# Revit family: IS_Gusto_BD420_BIM_NL
name_source: partatom
category: Plumbing Fixtures
units: mm (PartAtom-declared; Revit-internal decimal feet)

## family parameters
Always vertical = No
Cut with Voids When Loaded = No
OmniClass Number = 23.45.55.17
OmniClass Title = Mixing Faucets
Part Type = Normal
Room Calculation Point = No
Round Connector Dimension = Use Diameter
Shared = No
Work Plane-Based = No

## types (5) — shared parameters
Accessories = https://www.idealstandard.nl
Afmetingen = 115 x 275 x 333 mm
AfstandsEenheid = Millimeter
AreaUnits = millimetres
AssetType = Fixed
Auteur = Ideal Standard
BIMObjectName = IS_IdealStandard_Sinktaps_Gusto_BD420
BIMobject category = Taps & Mixers
BIMobject category code = sanitary-taps-mixers
BIMobject main category = Sanitary
BIMobject main category code = sanitary
Bedieningkraan = Einhebel
Bedieningkraanwerk = Einhebel
BeschrijvingBovenkantKraan = 2 Funktionen
Beschrijvinggarantie = Herstellergarantie
Bestanddelen = https://www.idealstandard.nl
BimObjectNaam = IS_IdealStandard_Sinktaps_Gusto_BD420
Brand = Ideal Standard
Brand url = http://www.idealstandard.nl
Breedte = 114.50873
Category = Taps & Mixers
ConnectionType = Plumbing
CurrencyUnit = €
CurrentRevision = 1
Date of publishing = 19/08/2022
Diepte = 275 mm
DurationUnit = Years
DuurEenheid = Jahre
Edition number = 1
ExpectedLife = 5
FaucetFunction = Sink Mixer
FaucetOperation = Single Lever Sink Mixer
FaucetTopDescription = Single lever
FaucetType = Sink Mixer
Functiekraanwerk = Küchenmischer
GTIN code = https://3800861108900
Garantieunits = Jahre
Help = https://www.idealstandard.nl
Hoogte = 333.311406525318
Hulp = https://www.idealstandard.nl
IFC Classification = Sanitary Terminal
Installatieinstructies = https://www.idealstandard.nl
Installation instructions = https://www.idealstandard.nl
InstallationInstructions = https://www.idealstandard.nl
Lengte = 275 mm
LinearUnits = millimetres
MaintenanceInformation = https://www.idealstandard.nl
Manufacturer = Ideal Standard
Manufacturer name = Ideal Standard
ManufacturerURL = http://www.idealstandard.nl
Masterformat 2014 Code = 22 41 16.16
Masterformat 2014 Description = Residential Sink
Materiaal = Messing
Material = Brass
Material main = Brass
Merk = Ideal Standard
NBS Reference Code = 45-35-70/345
NBS Reference Description = Water supply fittings for sinks
Name = Sinktaps_Gusto_BD420_IdealStandard
NettWeight = 3.04 Kg
Nettogewicht = 3.04
NominalDepth = 275 mm
NominalHeight = 333 mm
NominalLength = 275 mm
NominalWidth = 115 mm
Normen = Sinktaps_Gusto_BD420_IdealStandard
OmniClass Code = 23-31 11 00
OmniClass Description = Faucets
OppervlakteEenheid = Millimeter
PredefinedType = Taps & Mixers
Product Guid = 19f92fd7-092d-42a8-8991-9b57957d70f6
Product SKU = BD420
Product certification = https://www.idealstandard.nl
Product data url = https://bimobject.com
Product family = Gusto
Product group = Taps & Mixers
Product name = GUSTO SLIM SINK MIXER P/O 2 FUNTIONS BLUE START
Product url = https://www.idealstandard.nl
ProductInformation = https://www.idealstandard.nl
Productinformatie = https://www.idealstandard.nl
QR code = http://bimobject.com
Revisie = 1
Shape = Cylindrical
Size = 115 x 275 x 333 mm
Space = Internal
SpareParts = https://www.idealstandard.nl
Technical description = https://www.idealstandard.nl
Telefoonnummer = (0228) 521-580
Toepassing = Küchenmischer
Type Comments = Plumbing
Typeconnectie = Installation
Typekraanwerk = Einhebelmischer
UNSPSC Code = 301815
URL = https://www.idealstandard.nl
Uniclass 2015 Code = Pr_40_20_87_82
Uniclass 2015 Name = Sink manual water supply sets
Uniclass2015Beschrijving = Sink manual water supply sets
Uniclass2015Code = Pr_40_20_87_84
Uniclass2015Referentie = Pr_40_20_87_82
Uniclass2015Title = Sink taps
Uniclass2015Version = v1.26
Urlproducent = https://www.idealstandard.nl
ValutaEenheid = Euro
Versie = 1
Version = 1
VolumeUnits = Liters
Volumeunits = Liter
Vorm = Zylinder
WRASURL = https://www.wrasapprovals.co.uk
WarrantyDescription = manufacturer warranty
WarrantyDurationParts = 5
WarrantyDurationUnit = Years
WarrantyStartDate = 19/08/2022
Weight Net (Kg) = 3.04
Wisselstukken = https://www.idealstandard.nl
Youtube clip = https://www.youtube.com
zero-valued in all types: BrutoGewicht, Cost, Vervangingskosten

## per-type parameters (varying)
| type | Afwerking | Artikelnummer | Artikelomschrijving | Artikelreferentie | BarCode | Barcode | Color | Description | Eigenschappen | Features | Finish | Kleur | MainColor | Model | ModelNumber | ModelReference |
| BD420A5 - Gusto slim sink mixer p/o 2 funtions blue start - Magnetic Grey | Magnetisches Grau | BD420A5 | Gusto Slim Spültischmischer p/o 2 funtions blue start - Magnetic Grey | Gusto Slim Spültischmischer p/o 2 funtions blue start - Magnetic Grey | 3800861109150 | 3800861109150 | Magnetic Grey | Gusto slim sink mixer p/o 2 funtions blue start - Magnetic Grey | Slim Spültischmischer p/o 2 funtions blue start - Magnetic Grey | Slim Sink mixer p/o 2 funtions blue start - Magnetic Grey | Magnetic Grey | Magnetisches Grau | Magnetic Grey | BD420A5 | BD420A5 | Gusto slim sink mixer p/o 2 funtions blue start |
| BD420AA - Gusto slim sink mixer rim mounted p/o 2 funtions blue start - Chrome | Chrom | BD420AA | Gusto Slim Spültischmischer Wannenrandmontage p/o 2 funtions blue start - Chrom | Gusto Slim Spültischmischer Wannenrandmontage p/o 2 funtions blue start - Chrom | 3800861108696 | 3800861108696 | Chrome | Gusto slim sink mixer rim mounted p/o 2 funtions blue start - Chrome | Slim Spültischmischer randmontiert p/o 2 funtions blue start - Chrom | Slim Sink mixer rim mounted p/o 2 funtions blue start - Chrome | Chrome | Chrom | Chrome | BD420AA | BD420AA | Gusto slim sink mixer rim mounted p/o 2 funtions blue start |
| BD420GN - Gusto slim sink mixer p/o 2 funtions blue start - Silver | Silber | BD420GN | Gusto Slim Spültischmischer p/o 2 funtions blue start - Silver | Gusto Slim Spültischmischer p/o 2 funtions blue start - Silver | 3800861108894 | 3800861108894 | Silver | Gusto slim sink mixer p/o 2 funtions blue start - Silver | Slim Spültischmischer p/o 2 funtions blue start - Silver | Slim Sink mixer p/o 2 funtions blue start - Silver | Silver | Silber | Silver | BD420GN | BD420GN | Gusto slim sink mixer p/o 2 funtions blue start |
| BD420J4 - Gusto slim sink mixer p/o 2 funtions blue start - Brushed Copper | Gebürstetes Kupfer | BD420J4 | Gusto Slim Spültischmischer p/o 2 funtions blue start - Brushed Copper | Gusto Slim Spültischmischer p/o 2 funtions blue start - Brushed Copper | 3800861109310 | 3800861109310 | Brushed Copper | Gusto slim sink mixer p/o 2 funtions blue start - Brushed Copper | Slim Spültischmischer p/o 2 funtions blue start - Brushed Copper | Slim Sink mixer p/o 2 funtions blue start - Brushed Copper | Brushed Copper | Gebürstetes Kupfer | Brushed Copper | BD420J4 | BD420J4 | Gusto slim sink mixer p/o 2 funtions blue start |
| BD420A2 - Gusto slim sink mixer p/o 2 funtions blue start - BrushedGold | Gebürstetes Gold | BD420A2 | Gusto Slim Spültischmischer p/o 2 funtions blue start - BrushedGold | Gusto Slim Spültischmischer p/o 2 funtions blue start - BrushedGold | 3800861108900 | 3800861108900 | BrushedGold | Gusto slim sink mixer p/o 2 funtions blue start - BrushedGold | Slim Spültischmischer p/o 2 funtions blue start - BrushedGold | Slim Sink mixer p/o 2 funtions blue start - BrushedGold | BrushedGold | Gebürstetes Gold | BrushedGold | BD420A2 | BD420A2 | Gusto slim sink mixer p/o 2 funtions blue start |

## geometry (parser evidence)
native form markers: Sweep x1
no freeform markers — native parametric forms only
